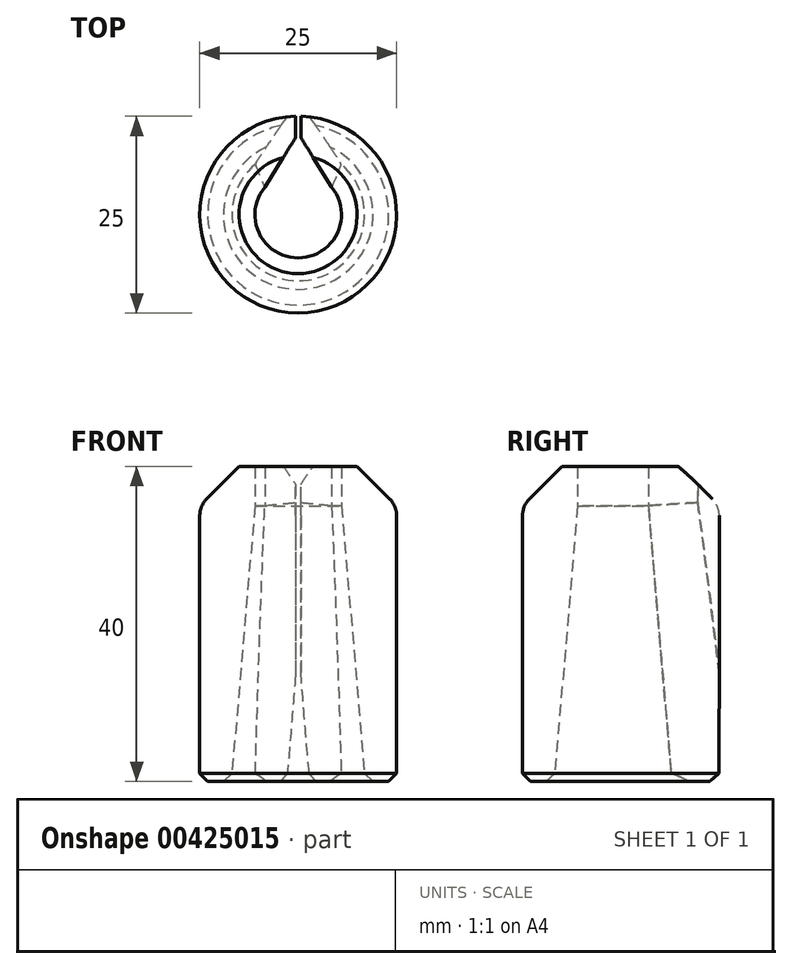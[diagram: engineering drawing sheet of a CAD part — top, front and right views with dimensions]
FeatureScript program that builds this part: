
annotation { "Feature Type Name" : "Feature", "Feature Type Description" : "" }
export const myFeature = defineFeature(function(context is Context, id is Id, definition is map)
    precondition{}
    {
        {
            var Q0;
            Q0=qCreatedBy(makeId("Top.planeOp"),FACE);
            var sketch = newSketch(context, id + "F0", { "sketchPlane" : qUnion([Q0])});
            skCircle(sketch, "E0", {"center": v(0, 0) * mm, "radius": 12.5 * mm});
            skCircle(sketch, "E1.0", {"center": v(0, 0) * mm, "radius": 5.5 * mm});
            skSolve(sketch);
        }
        {
            var Q0;
            Q0=makeQuery(id+"F0.imprint","IMPRINT",FACE,{"disambiguationData":[TD([[makeQuery(id+"F0.imprint","IMPRINT",EDGE,{"derivedFrom":sQuery(id+"F0.wireOp",EDGE,"E0")}),1.0]])]});
            extrude(context, id + "F1", {"entities" : qUnion([Q0]), "offsetDistance" : 25 * mm, "depth" : 40 * mm});
        }
        {
            var Q0;
            Q0=makeQuery(id+"F1.opExtrude","CAP_EDGE",EDGE,{"disambiguationData":[OSD([sQuery(id+"F0.wireOp",EDGE,"E0")])],"isStart":false});
            chamfer(context, id + "F2", {"entities" : qUnion([Q0]), "width" : 5 * mm, "tangentPropagation" : true});
        }
        {
            var Q0;
            {var subQ0=sQuery(id+"F0.wireOp",EDGE,"E0");Q0=makeQuery(id+"F2.opChamfer","BLEND_EDGE",EDGE,{"blendedFrom":[makeQuery(id+"F1.opExtrude","CAP_EDGE",EDGE,{"disambiguationData":[OSD([subQ0])],"isStart":false}),makeQuery(id+"F1.opExtrude","SWEPT_FACE",FACE,{"disambiguationData":[OSD([subQ0])]})],"blendedInto":[makeQuery(id+"F1.opExtrude","SWEPT_FACE",FACE,{"disambiguationData":[OSD([subQ0])]})]});}
            fillet(context, id + "F3", {"entities" : qUnion([Q0]), "radius" : 3 * mm, "tangentPropagation" : true, "allowEdgeOverflow" : false});
        }
        {
            var Q0;
            Q0=makeQuery(id+"F1.opExtrude","CAP_EDGE",EDGE,{"disambiguationData":[OSD([sQuery(id+"F0.wireOp",EDGE,"E1.0")])],"isStart":true});
            chamfer(context, id + "F4", {"entities" : qUnion([Q0]), "chamferType" : ChamferType.TWO_OFFSETS, "width1" : 3 * mm, "oppositeDirection" : false, "width2" : 35 * mm, "tangentPropagation" : true});
        }
        {
            var Q0;
            Q0=qCreatedBy(makeId("Front.planeOp"),FACE);
            var sketch = newSketch(context, id + "F5", { "sketchPlane" : qUnion([Q0])});
            skLineSegment(sketch, "E2.bottom", {"start": v(-0.34, 40.4) * mm, "end": v(0.36, 40.4) * mm});
            skLineSegment(sketch, "E2.top", {"start": v(-0.34, -1.1) * mm, "end": v(0.36, -1.1) * mm});
            skLineSegment(sketch, "E2.left", {"start": v(-0.34, 40.4) * mm, "end": v(-0.34, -1.1) * mm});
            skLineSegment(sketch, "E2.right", {"start": v(0.36, 40.4) * mm, "end": v(0.36, -1.1) * mm});
            skSolve(sketch);
        }
        {
            var Q0;
            Q0=makeQuery(id+"F5.imprint","IMPRINT",FACE,{"disambiguationData":[TD([[makeQuery(id+"F5.imprint","IMPRINT",EDGE,{"derivedFrom":sQuery(id+"F5.wireOp",EDGE,"E2.bottom")}),-1.0]])]});
            extrude(context, id + "F6", {"entities" : qUnion([Q0]), "operationType" : NewBodyOperationType.REMOVE, "oppositeDirection" : true, "depth" : 25 * mm, "offsetDistance" : 25 * mm});
        }
        {
            var Q0;
            Q0=makeQuery(id+"F6.boolean.opBoolean","INTERSECT",EDGE,{"derivedFrom":[makeQuery(id+"F4.opChamfer","BLEND_FACE",FACE,{"disambiguationData":[OSD([sQuery(id+"F0.wireOp",EDGE,"E1.0")])]}),makeQuery(id+"F6.opExtrude","SWEPT_FACE",FACE,{"disambiguationData":[OSD([sQuery(id+"F5.wireOp",EDGE,"E2.right")])]})]});
            var Q1;
            Q1=makeQuery(id+"F6.boolean.opBoolean","INTERSECT",EDGE,{"derivedFrom":[makeQuery(id+"F4.opChamfer","BLEND_FACE",FACE,{"disambiguationData":[OSD([sQuery(id+"F0.wireOp",EDGE,"E1.0")])]}),makeQuery(id+"F6.opExtrude","SWEPT_FACE",FACE,{"disambiguationData":[OSD([sQuery(id+"F5.wireOp",EDGE,"E2.left")])]})]});
            var Q2;
            Q2=makeQuery(id+"F6.boolean.opBoolean","INTERSECT",EDGE,{"derivedFrom":[makeQuery(id+"F1.opExtrude","SWEPT_FACE",FACE,{"disambiguationData":[OSD([sQuery(id+"F0.wireOp",EDGE,"E1.0")])]}),makeQuery(id+"F6.opExtrude","SWEPT_FACE",FACE,{"disambiguationData":[OSD([sQuery(id+"F5.wireOp",EDGE,"E2.right")])]})]});
            var Q3;
            Q3=makeQuery(id+"F6.boolean.opBoolean","INTERSECT",EDGE,{"derivedFrom":[makeQuery(id+"F1.opExtrude","SWEPT_FACE",FACE,{"disambiguationData":[OSD([sQuery(id+"F0.wireOp",EDGE,"E1.0")])]}),makeQuery(id+"F6.opExtrude","SWEPT_FACE",FACE,{"disambiguationData":[OSD([sQuery(id+"F5.wireOp",EDGE,"E2.left")])]})]});
            chamfer(context, id + "F7", {"entities" : qUnion([Q0, Q1, Q2, Q3]), "width" : 5 * mm, "tangentPropagation" : true});
        }
        {
            var Q0;
            {var subQ0=sQuery(id+"F0.wireOp",EDGE,"E1.0");Q0=makeQuery(id+"F4.opChamfer","BLEND_EDGE",EDGE,{"blendedFrom":[makeQuery(id+"F1.opExtrude","CAP_EDGE",EDGE,{"disambiguationData":[OSD([subQ0])],"isStart":true}),makeQuery(id+"F1.opExtrude","CAP_FACE",FACE,{"disambiguationData":[OSD([sQuery(id+"F0.wireOp",EDGE,"E0"),subQ0])],"isStart":true})],"blendedInto":[makeQuery(id+"F1.opExtrude","CAP_FACE",FACE,{"disambiguationData":[OSD([sQuery(id+"F0.wireOp",EDGE,"E0"),subQ0])],"isStart":true})]});}
            var Q1;
            Q1=makeQuery(id+"F1.opExtrude","CAP_EDGE",EDGE,{"disambiguationData":[OSD([sQuery(id+"F0.wireOp",EDGE,"E0")])],"isStart":true});
            chamfer(context, id + "F8", {"entities" : qUnion([Q0, Q1]), "width" : 1 * mm, "tangentPropagation" : true});
        }
    });
